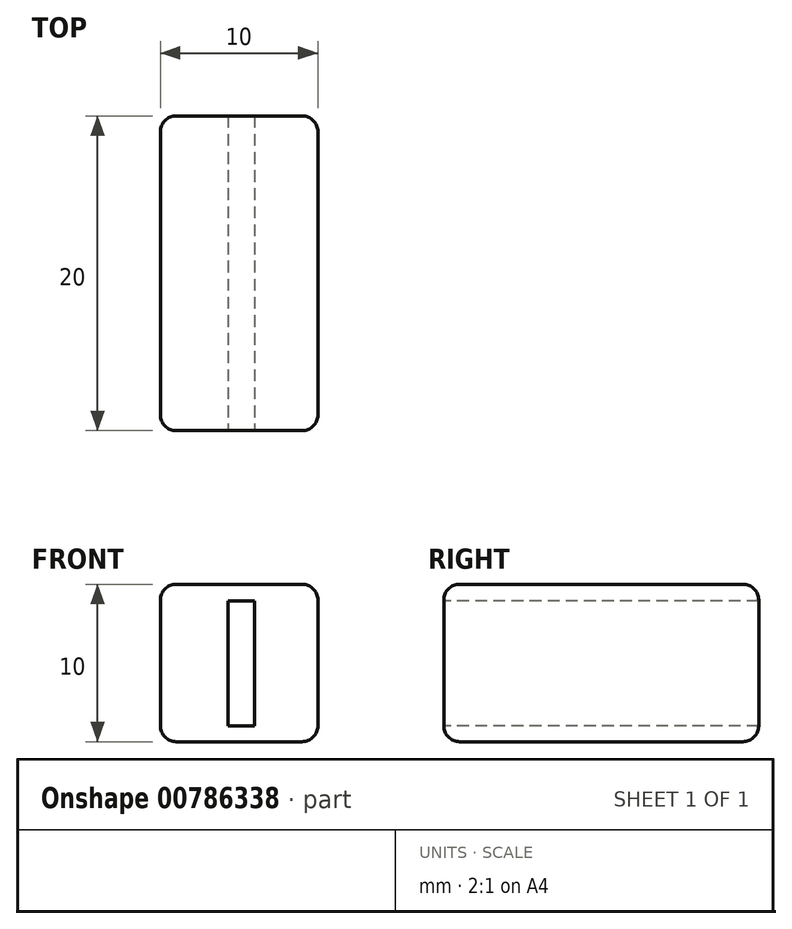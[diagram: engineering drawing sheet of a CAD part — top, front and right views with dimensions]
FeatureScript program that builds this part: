
annotation { "Feature Type Name" : "Feature", "Feature Type Description" : "" }
export const myFeature = defineFeature(function(context is Context, id is Id, definition is map)
    precondition{}
    {
        {
            var Q0;
            Q0=qCreatedBy(makeId("Front.planeOp"),FACE);
            var sketch = newSketch(context, id + "F0", { "sketchPlane" : qUnion([Q0])});
            skLineSegment(sketch, "E0.bottom", {"start": v(0, 0) * mm, "end": v(10, 0) * mm});
            skLineSegment(sketch, "E0.top", {"start": v(0, 10) * mm, "end": v(10, 10) * mm});
            skLineSegment(sketch, "E0.left", {"start": v(0, 0) * mm, "end": v(0, 10) * mm});
            skLineSegment(sketch, "E0.right", {"start": v(10, 0) * mm, "end": v(10, 10) * mm});
            skSolve(sketch);
        }
        {
            var Q0;
            Q0 = qSketchRegion(id + "F0", true);
            extrude(context, id + "F1", {"entities" : qUnion([Q0]), "depth" : 20 * mm, "offsetDistance" : 25 * mm});
        }
        {
            var Q0;
            Q0=makeQuery(id+"F1.opExtrude","SWEPT_FACE",FACE,{"disambiguationData":[OSD([sQuery(id+"F0.wireOp",EDGE,"E0.top")])]});
            var Q1;
            Q1=makeQuery(id+"F1.opExtrude","SWEPT_FACE",FACE,{"disambiguationData":[OSD([sQuery(id+"F0.wireOp",EDGE,"E0.right")])]});
            var Q2;
            Q2=makeQuery(id+"F1.opExtrude","SWEPT_FACE",FACE,{"disambiguationData":[OSD([sQuery(id+"F0.wireOp",EDGE,"E0.bottom")])]});
            var Q3;
            Q3=makeQuery(id+"F1.opExtrude","SWEPT_FACE",FACE,{"disambiguationData":[OSD([sQuery(id+"F0.wireOp",EDGE,"E0.left")])]});
            fillet(context, id + "F2", {"entities" : qUnion([Q0, Q1, Q2, Q3]), "radius" : 1 * mm, "tangentPropagation" : true, "allowEdgeOverflow" : false});
        }
        {
            var Q0;
            Q0=makeQuery(id+"F1.opExtrude","CAP_FACE",FACE,{"disambiguationData":[OSD([sQuery(id+"F0.wireOp",EDGE,"E0.bottom"),sQuery(id+"F0.wireOp",EDGE,"E0.top"),sQuery(id+"F0.wireOp",EDGE,"E0.left"),sQuery(id+"F0.wireOp",EDGE,"E0.right")])],"isStart":false});
            var sketch = newSketch(context, id + "F3", { "sketchPlane" : qUnion([Q0])});
            skText(sketch, "E1", { "text": "I", "fontName": "OpenSans-Bold.ttf"});
            const initialGuessF3  = {"E1": [0.0033, 0.001, 1, 0, 0.008]};
            skSetInitialGuess(sketch, initialGuessF3);
            skSolve(sketch);
        }
        {
            var Q0;
            Q0 = qSketchRegion(id + "F3", true);
            extrude(context, id + "F4", {"entities" : qUnion([Q0]), "operationType" : NewBodyOperationType.REMOVE, "oppositeDirection" : true, "depth" : 20 * mm, "offsetDistance" : 25 * mm});
        }
    });
